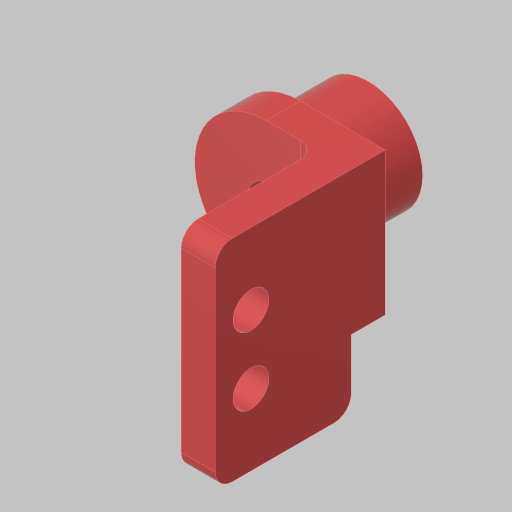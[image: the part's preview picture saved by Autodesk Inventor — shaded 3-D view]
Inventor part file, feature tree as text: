
AUTODESK INVENTOR PART (.ipt)
format: ipt  version: 2023.5 (Build 275446000, 446)  size: 158,720 bytes
history: native  units: in
note: dims shown in document units (in); Inventor stores cm internally (conversion verified against a paired STEP export)
features: sketch x5, extrude x3, hole x2, fillet x1, projected_geometry x1
ambient origin geometry x8: Origin, YZ Plane, XZ Plane, XY Plane, X Axis, Y Axis, Z Axis, Center Point
bodies: Solid1 (feature_tree)
feature tree (12):
  extrude  "Extrusion1"  Depth=0.5in TaperAngle=0.0deg
  extrude  "Extrusion2"  Depth=0.25in TaperAngle=0.0deg
  hole  "Hole2"  [1 undecoded]
  extrude  "Extrusion3"  Depth=0.25in
  fillet  "Fillet1"  Radius=1.0in
  hole  "Hole3"  [1 undecoded]
  sketch  "Sketch1"  dims[d0=0.8in d1=0.5in d2=0.0in]
  sketch  "Sketch2"  dims[d3=0.125in d4=0.25in d5=0.0in]
  sketch  "Sketch4"  dims[d6=0.688in d14=0.625in]
  sketch  "Sketch5"  dims[d15=0.257in d16=0.75in d17=0.375in d18=0.25in d19=0.5635in d20=1.0in d21=0.8108in d22=0.25in d23=1.0in d24=0.0in]
  sketch  "Sketch6"  dims[d25=0.125in d26=0.5in d27=0.2638in d28=0.38in d29=0.385in d30=0.25in d31=0.5635in d32=1.0in d33=0.8108in d35=0.525in d36=0.5in d37=0.263in]
  projected_geometry  "Project Cut Edges1"
note: 2 required parameter values undecoded (feature->parameter linkage not recoverable at this tier; creation-order binding heuristic only, values carry confidence <= 0.55)
